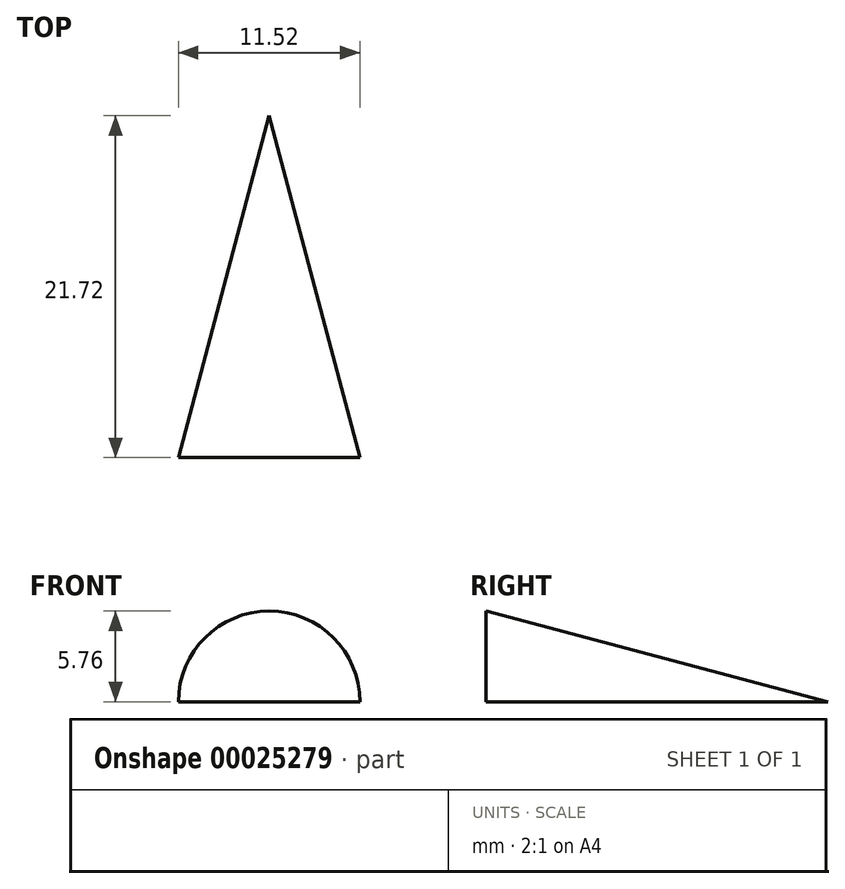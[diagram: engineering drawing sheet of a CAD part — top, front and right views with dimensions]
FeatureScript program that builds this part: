
annotation { "Feature Type Name" : "Feature", "Feature Type Description" : "" }
export const myFeature = defineFeature(function(context is Context, id is Id, definition is map)
    precondition{}
    {
        {
            var Q0;
            Q0=qCreatedBy(makeId("Top.planeOp"),FACE);
            var sketch = newSketch(context, id + "F0", { "sketchPlane" : qUnion([Q0])});
            skLineSegment(sketch, "E0", {"start": v(-5.69, 0) * mm, "end": v(5.76, 0) * mm});
            skLineSegment(sketch, "E1", {"start": v(5.76, 0) * mm, "end": v(0, 21.72) * mm});
            skLineSegment(sketch, "E2", {"start": v(0, 21.72) * mm, "end": v(-5.69, 0) * mm});
            skLineSegment(sketch, "E3", {"start": v(0, 21.72) * mm, "end": v(0, 0) * mm});
            skSolve(sketch);
        }
        {
            var Q0;
            {var subQ1=sQuery(id+"F0.wireOp",EDGE,"E1");Q0=makeQuery(id+"F0.imprint","IMPRINT",FACE,{"disambiguationData":[TD([[makeQuery(id+"F0.imprint","IMPRINT",EDGE,{"derivedFrom":subQ1}),1.0]])]});}
            var Q1;
            Q1=sQuery(id+"F0.wireOp",EDGE,"E3");
            revolve(context, id + "F1", {"entities" : qUnion([Q0]), "axis" : qUnion([Q1]), "revolveType" : RevolveType.ONE_DIRECTION, "angle" : 180 * degree});
        }
    });
